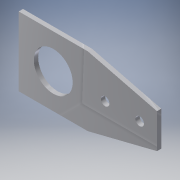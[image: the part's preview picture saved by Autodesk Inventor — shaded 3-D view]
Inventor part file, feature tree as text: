
AUTODESK INVENTOR PART (.ipt)
format: ipt  version: 2016 (Build 200138000, 138)  size: 112,640 bytes
history: native  units: in
note: dims shown in document units (in); Inventor stores cm internally (conversion verified against a paired STEP export)
features: extrude x1, sketch x1
ambient origin geometry x8: Origin, YZ Plane, XZ Plane, XY Plane, X Axis, Y Axis, Z Axis, Center Point
bodies: Solid1 (feature_tree)
feature tree (2):
  extrude  "Extrusion1"  Depth=2.0in
  sketch  "Sketch1"  dims[d1=2.0in d2=2.0in d3=2.0in d4=1.0in d5=1.125in d6=1.0in d7=1.0in d8=0.25in d9=0.25in d10=0.5in d11=1.0in d12=0.125in d13=0.0in]
